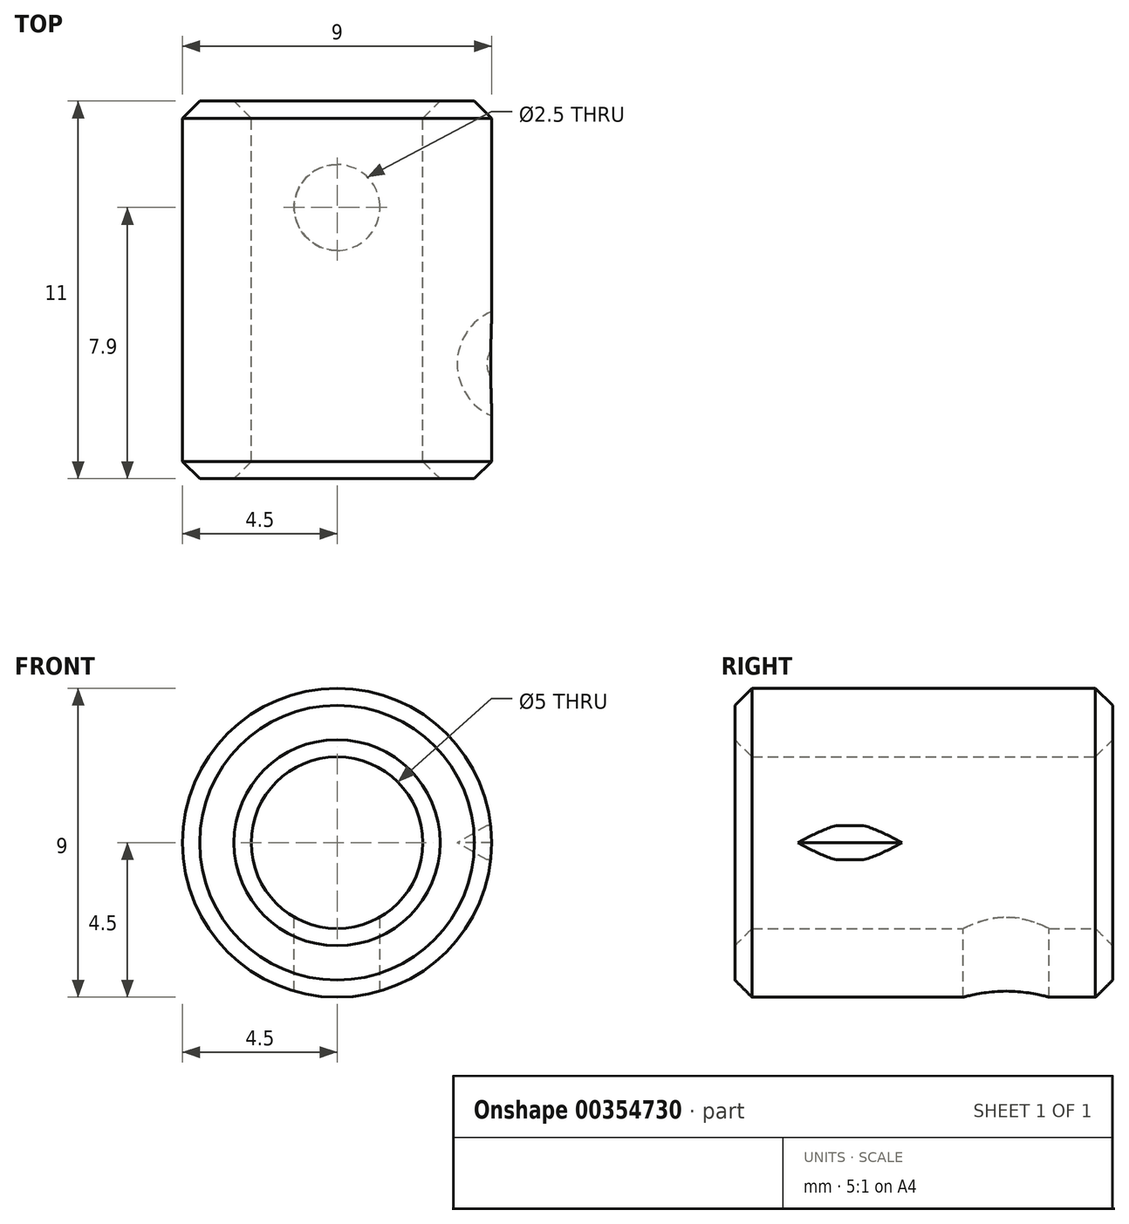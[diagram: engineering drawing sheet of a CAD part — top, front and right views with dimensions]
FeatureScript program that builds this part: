
annotation { "Feature Type Name" : "Feature", "Feature Type Description" : "" }
export const myFeature = defineFeature(function(context is Context, id is Id, definition is map)
    precondition{}
    {
        {
            var Q0;
            Q0=qCreatedBy(makeId("Front.planeOp"),FACE);
            var sketch = newSketch(context, id + "F0", { "sketchPlane" : qUnion([Q0])});
            skCircle(sketch, "E0", {"center": v(0, 0) * mm, "radius": 4.5 * mm});
            skCircle(sketch, "E1", {"center": v(0, 0) * mm, "radius": 2.5 * mm});
            skSolve(sketch);
        }
        {
            var Q0;
            Q0=qSketchRegion(id+"F0",true);
            extrude(context, id + "F1", {"entities" : qUnion([Q0]), "depth" : 11 * mm});
        }
        {
            var Q0;
            Q0=qCreatedBy(makeId("Top.planeOp"),FACE);
            var sketch = newSketch(context, id + "F2", { "sketchPlane" : qUnion([Q0])});
            skCircle(sketch, "E2", {"center": v(5.15, -7.65) * mm, "radius": 1.65 * mm});
            skLineSegment(sketch, "E3", {"start": v(0, -26.8) * mm, "end": v(0, 9.04) * mm, "construction": true});
            skSolve(sketch);
        }
        {
            var Q0;
            Q0=qSketchRegion(id+"F2",true);
            extrude(context, id + "F3", {"entities" : qUnion([Q0]), "endBound" : BoundingType.SYMMETRIC, "depth" : 1 * mm, "hasDraft" : true, "draftAngle" : 60 * degree, "draftPullDirection" : true});
        }
        {
            var Q0;
            Q0=makeQuery(id+"FlCykohCmPU6IM3_2.11.F3.*.split.splitOp","SPLIT",BODY,{"derivedFrom":makeQuery(id+"FlCykohCmPU6IM3_2.11.F3.opExtrude","SWEPT_BODY",BODY,{"disambiguationData":[OSD([sQuery(id+"F2.wireOp",EDGE,"E2")])]})});
            var Q1;
            Q1=makeQuery(id+"FlCykohCmPU6IM3_2.2.F3.*.split.splitOp","SPLIT",BODY,{"derivedFrom":makeQuery(id+"FlCykohCmPU6IM3_2.2.F3.opExtrude","SWEPT_BODY",BODY,{"disambiguationData":[OSD([sQuery(id+"F2.wireOp",EDGE,"E2")])]})});
            var Q2;
            Q2=makeQuery(id+"FlCykohCmPU6IM3_2.1.F3.*.split.splitOp","SPLIT",BODY,{"derivedFrom":makeQuery(id+"FlCykohCmPU6IM3_2.1.F3.opExtrude","SWEPT_BODY",BODY,{"disambiguationData":[OSD([sQuery(id+"F2.wireOp",EDGE,"E2")])]})});
            var Q3;
            Q3=makeQuery(id+"FlCykohCmPU6IM3_2.10.F3.*.split.splitOp","SPLIT",BODY,{"derivedFrom":makeQuery(id+"FlCykohCmPU6IM3_2.10.F3.opExtrude","SWEPT_BODY",BODY,{"disambiguationData":[OSD([sQuery(id+"F2.wireOp",EDGE,"E2")])]})});
            var Q4;
            Q4=makeQuery(id+"FlCykohCmPU6IM3_2.13.F3.*.split.splitOp","SPLIT",BODY,{"derivedFrom":makeQuery(id+"FlCykohCmPU6IM3_2.13.F3.opExtrude","SWEPT_BODY",BODY,{"disambiguationData":[OSD([sQuery(id+"F2.wireOp",EDGE,"E2")])]})});
            var Q5;
            Q5=makeQuery(id+"FlCykohCmPU6IM3_2.5.F3.*.split.splitOp","SPLIT",BODY,{"derivedFrom":makeQuery(id+"FlCykohCmPU6IM3_2.5.F3.opExtrude","SWEPT_BODY",BODY,{"disambiguationData":[OSD([sQuery(id+"F2.wireOp",EDGE,"E2")])]})});
            var Q6;
            Q6=makeQuery(id+"FlCykohCmPU6IM3_2.9.F3.*.split.splitOp","SPLIT",BODY,{"derivedFrom":makeQuery(id+"FlCykohCmPU6IM3_2.9.F3.opExtrude","SWEPT_BODY",BODY,{"disambiguationData":[OSD([sQuery(id+"F2.wireOp",EDGE,"E2")])]})});
            var Q7;
            Q7=makeQuery(id+"FlCykohCmPU6IM3_2.6.F3.*.split.splitOp","SPLIT",BODY,{"derivedFrom":makeQuery(id+"FlCykohCmPU6IM3_2.6.F3.opExtrude","SWEPT_BODY",BODY,{"disambiguationData":[OSD([sQuery(id+"F2.wireOp",EDGE,"E2")])]})});
            var Q8;
            Q8=makeQuery(id+"FlCykohCmPU6IM3_2.14.F3.*.split.splitOp","SPLIT",BODY,{"derivedFrom":makeQuery(id+"FlCykohCmPU6IM3_2.14.F3.opExtrude","SWEPT_BODY",BODY,{"disambiguationData":[OSD([sQuery(id+"F2.wireOp",EDGE,"E2")])]})});
            var Q9;
            Q9=makeQuery(id+"FlCykohCmPU6IM3_2.19.F3.*.split.splitOp","SPLIT",BODY,{"derivedFrom":makeQuery(id+"FlCykohCmPU6IM3_2.19.F3.opExtrude","SWEPT_BODY",BODY,{"disambiguationData":[OSD([sQuery(id+"F2.wireOp",EDGE,"E2")])]})});
            var Q10;
            Q10=makeQuery(id+"FlCykohCmPU6IM3_2.4.F3.*.split.splitOp","SPLIT",BODY,{"derivedFrom":makeQuery(id+"FlCykohCmPU6IM3_2.4.F3.opExtrude","SWEPT_BODY",BODY,{"disambiguationData":[OSD([sQuery(id+"F2.wireOp",EDGE,"E2")])]})});
            var Q11;
            Q11=makeQuery(id+"F3.*.split.splitOp","SPLIT",BODY,{"derivedFrom":makeQuery(id+"F3.opExtrude","SWEPT_BODY",BODY,{"disambiguationData":[OSD([sQuery(id+"F2.wireOp",EDGE,"E2")])]})});
            var Q12;
            Q12=makeQuery(id+"FlCykohCmPU6IM3_2.3.F3.*.split.splitOp","SPLIT",BODY,{"derivedFrom":makeQuery(id+"FlCykohCmPU6IM3_2.3.F3.opExtrude","SWEPT_BODY",BODY,{"disambiguationData":[OSD([sQuery(id+"F2.wireOp",EDGE,"E2")])]})});
            var Q13;
            Q13=makeQuery(id+"FlCykohCmPU6IM3_2.7.F3.*.split.splitOp","SPLIT",BODY,{"derivedFrom":makeQuery(id+"FlCykohCmPU6IM3_2.7.F3.opExtrude","SWEPT_BODY",BODY,{"disambiguationData":[OSD([sQuery(id+"F2.wireOp",EDGE,"E2")])]})});
            var Q14;
            Q14=makeQuery(id+"FlCykohCmPU6IM3_2.33.F3.*.split.splitOp","SPLIT",BODY,{"derivedFrom":makeQuery(id+"FlCykohCmPU6IM3_2.33.F3.opExtrude","SWEPT_BODY",BODY,{"disambiguationData":[OSD([sQuery(id+"F2.wireOp",EDGE,"E2")])]})});
            var Q15;
            Q15=makeQuery(id+"FlCykohCmPU6IM3_2.32.F3.*.split.splitOp","SPLIT",BODY,{"derivedFrom":makeQuery(id+"FlCykohCmPU6IM3_2.32.F3.opExtrude","SWEPT_BODY",BODY,{"disambiguationData":[OSD([sQuery(id+"F2.wireOp",EDGE,"E2")])]})});
            var Q16;
            Q16=makeQuery(id+"FlCykohCmPU6IM3_2.31.F3.*.split.splitOp","SPLIT",BODY,{"derivedFrom":makeQuery(id+"FlCykohCmPU6IM3_2.31.F3.opExtrude","SWEPT_BODY",BODY,{"disambiguationData":[OSD([sQuery(id+"F2.wireOp",EDGE,"E2")])]})});
            var Q17;
            Q17=makeQuery(id+"FlCykohCmPU6IM3_2.30.F3.*.split.splitOp","SPLIT",BODY,{"derivedFrom":makeQuery(id+"FlCykohCmPU6IM3_2.30.F3.opExtrude","SWEPT_BODY",BODY,{"disambiguationData":[OSD([sQuery(id+"F2.wireOp",EDGE,"E2")])]})});
            var Q18;
            Q18=makeQuery(id+"FlCykohCmPU6IM3_2.29.F3.*.split.splitOp","SPLIT",BODY,{"derivedFrom":makeQuery(id+"FlCykohCmPU6IM3_2.29.F3.opExtrude","SWEPT_BODY",BODY,{"disambiguationData":[OSD([sQuery(id+"F2.wireOp",EDGE,"E2")])]})});
            var Q19;
            Q19=makeQuery(id+"FlCykohCmPU6IM3_2.28.F3.*.split.splitOp","SPLIT",BODY,{"derivedFrom":makeQuery(id+"FlCykohCmPU6IM3_2.28.F3.opExtrude","SWEPT_BODY",BODY,{"disambiguationData":[OSD([sQuery(id+"F2.wireOp",EDGE,"E2")])]})});
            var Q20;
            Q20=makeQuery(id+"FlCykohCmPU6IM3_2.27.F3.*.split.splitOp","SPLIT",BODY,{"derivedFrom":makeQuery(id+"FlCykohCmPU6IM3_2.27.F3.opExtrude","SWEPT_BODY",BODY,{"disambiguationData":[OSD([sQuery(id+"F2.wireOp",EDGE,"E2")])]})});
            var Q21;
            Q21=makeQuery(id+"FlCykohCmPU6IM3_2.26.F3.*.split.splitOp","SPLIT",BODY,{"derivedFrom":makeQuery(id+"FlCykohCmPU6IM3_2.26.F3.opExtrude","SWEPT_BODY",BODY,{"disambiguationData":[OSD([sQuery(id+"F2.wireOp",EDGE,"E2")])]})});
            var Q22;
            Q22=makeQuery(id+"FlCykohCmPU6IM3_2.25.F3.*.split.splitOp","SPLIT",BODY,{"derivedFrom":makeQuery(id+"FlCykohCmPU6IM3_2.25.F3.opExtrude","SWEPT_BODY",BODY,{"disambiguationData":[OSD([sQuery(id+"F2.wireOp",EDGE,"E2")])]})});
            var Q23;
            Q23=makeQuery(id+"FlCykohCmPU6IM3_2.24.F3.*.split.splitOp","SPLIT",BODY,{"derivedFrom":makeQuery(id+"FlCykohCmPU6IM3_2.24.F3.opExtrude","SWEPT_BODY",BODY,{"disambiguationData":[OSD([sQuery(id+"F2.wireOp",EDGE,"E2")])]})});
            var Q24;
            Q24=makeQuery(id+"FlCykohCmPU6IM3_2.23.F3.*.split.splitOp","SPLIT",BODY,{"derivedFrom":makeQuery(id+"FlCykohCmPU6IM3_2.23.F3.opExtrude","SWEPT_BODY",BODY,{"disambiguationData":[OSD([sQuery(id+"F2.wireOp",EDGE,"E2")])]})});
            var Q25;
            Q25=makeQuery(id+"FlCykohCmPU6IM3_2.22.F3.*.split.splitOp","SPLIT",BODY,{"derivedFrom":makeQuery(id+"FlCykohCmPU6IM3_2.22.F3.opExtrude","SWEPT_BODY",BODY,{"disambiguationData":[OSD([sQuery(id+"F2.wireOp",EDGE,"E2")])]})});
            var Q26;
            Q26=makeQuery(id+"FlCykohCmPU6IM3_2.21.F3.*.split.splitOp","SPLIT",BODY,{"derivedFrom":makeQuery(id+"FlCykohCmPU6IM3_2.21.F3.opExtrude","SWEPT_BODY",BODY,{"disambiguationData":[OSD([sQuery(id+"F2.wireOp",EDGE,"E2")])]})});
            var Q27;
            Q27=makeQuery(id+"FlCykohCmPU6IM3_2.20.F3.*.split.splitOp","SPLIT",BODY,{"derivedFrom":makeQuery(id+"FlCykohCmPU6IM3_2.20.F3.opExtrude","SWEPT_BODY",BODY,{"disambiguationData":[OSD([sQuery(id+"F2.wireOp",EDGE,"E2")])]})});
            var Q28;
            Q28=makeQuery(id+"FlCykohCmPU6IM3_2.12.F3.*.split.splitOp","SPLIT",BODY,{"derivedFrom":makeQuery(id+"FlCykohCmPU6IM3_2.12.F3.opExtrude","SWEPT_BODY",BODY,{"disambiguationData":[OSD([sQuery(id+"F2.wireOp",EDGE,"E2")])]})});
            var Q29;
            Q29=makeQuery(id+"FlCykohCmPU6IM3_2.8.F3.*.split.splitOp","SPLIT",BODY,{"derivedFrom":makeQuery(id+"FlCykohCmPU6IM3_2.8.F3.opExtrude","SWEPT_BODY",BODY,{"disambiguationData":[OSD([sQuery(id+"F2.wireOp",EDGE,"E2")])]})});
            var Q30;
            Q30=makeQuery(id+"FlCykohCmPU6IM3_2.16.F3.*.split.splitOp","SPLIT",BODY,{"derivedFrom":makeQuery(id+"FlCykohCmPU6IM3_2.16.F3.opExtrude","SWEPT_BODY",BODY,{"disambiguationData":[OSD([sQuery(id+"F2.wireOp",EDGE,"E2")])]})});
            var Q31;
            Q31=makeQuery(id+"FlCykohCmPU6IM3_2.15.F3.*.split.splitOp","SPLIT",BODY,{"derivedFrom":makeQuery(id+"FlCykohCmPU6IM3_2.15.F3.opExtrude","SWEPT_BODY",BODY,{"disambiguationData":[OSD([sQuery(id+"F2.wireOp",EDGE,"E2")])]})});
            var Q32;
            Q32=makeQuery(id+"FlCykohCmPU6IM3_2.17.F3.*.split.splitOp","SPLIT",BODY,{"derivedFrom":makeQuery(id+"FlCykohCmPU6IM3_2.17.F3.opExtrude","SWEPT_BODY",BODY,{"disambiguationData":[OSD([sQuery(id+"F2.wireOp",EDGE,"E2")])]})});
            var Q33;
            Q33=makeQuery(id+"FlCykohCmPU6IM3_2.18.F3.*.split.splitOp","SPLIT",BODY,{"derivedFrom":makeQuery(id+"FlCykohCmPU6IM3_2.18.F3.opExtrude","SWEPT_BODY",BODY,{"disambiguationData":[OSD([sQuery(id+"F2.wireOp",EDGE,"E2")])]})});
            var Q34;
            Q34=makeQuery(id+"FlCykohCmPU6IM3_2.34.F3.*.split.splitOp","SPLIT",BODY,{"derivedFrom":makeQuery(id+"FlCykohCmPU6IM3_2.34.F3.opExtrude","SWEPT_BODY",BODY,{"disambiguationData":[OSD([sQuery(id+"F2.wireOp",EDGE,"E2")])]})});
            var Q35;
            Q35=makeQuery(id+"FlCykohCmPU6IM3_2.47.F3.*.split.splitOp","SPLIT",BODY,{"derivedFrom":makeQuery(id+"FlCykohCmPU6IM3_2.47.F3.opExtrude","SWEPT_BODY",BODY,{"disambiguationData":[OSD([sQuery(id+"F2.wireOp",EDGE,"E2")])]})});
            var Q36;
            Q36=makeQuery(id+"FlCykohCmPU6IM3_2.35.F3.*.split.splitOp","SPLIT",BODY,{"derivedFrom":makeQuery(id+"FlCykohCmPU6IM3_2.35.F3.opExtrude","SWEPT_BODY",BODY,{"disambiguationData":[OSD([sQuery(id+"F2.wireOp",EDGE,"E2")])]})});
            var Q37;
            Q37=makeQuery(id+"FlCykohCmPU6IM3_2.40.F3.*.split.splitOp","SPLIT",BODY,{"derivedFrom":makeQuery(id+"FlCykohCmPU6IM3_2.40.F3.opExtrude","SWEPT_BODY",BODY,{"disambiguationData":[OSD([sQuery(id+"F2.wireOp",EDGE,"E2")])]})});
            var Q38;
            Q38=makeQuery(id+"FlCykohCmPU6IM3_2.42.F3.*.split.splitOp","SPLIT",BODY,{"derivedFrom":makeQuery(id+"FlCykohCmPU6IM3_2.42.F3.opExtrude","SWEPT_BODY",BODY,{"disambiguationData":[OSD([sQuery(id+"F2.wireOp",EDGE,"E2")])]})});
            var Q39;
            Q39=makeQuery(id+"FlCykohCmPU6IM3_2.39.F3.*.split.splitOp","SPLIT",BODY,{"derivedFrom":makeQuery(id+"FlCykohCmPU6IM3_2.39.F3.opExtrude","SWEPT_BODY",BODY,{"disambiguationData":[OSD([sQuery(id+"F2.wireOp",EDGE,"E2")])]})});
            var Q40;
            Q40=makeQuery(id+"FlCykohCmPU6IM3_2.44.F3.*.split.splitOp","SPLIT",BODY,{"derivedFrom":makeQuery(id+"FlCykohCmPU6IM3_2.44.F3.opExtrude","SWEPT_BODY",BODY,{"disambiguationData":[OSD([sQuery(id+"F2.wireOp",EDGE,"E2")])]})});
            var Q41;
            Q41=makeQuery(id+"FlCykohCmPU6IM3_2.46.F3.*.split.splitOp","SPLIT",BODY,{"derivedFrom":makeQuery(id+"FlCykohCmPU6IM3_2.46.F3.opExtrude","SWEPT_BODY",BODY,{"disambiguationData":[OSD([sQuery(id+"F2.wireOp",EDGE,"E2")])]})});
            var Q42;
            Q42=makeQuery(id+"FlCykohCmPU6IM3_2.45.F3.*.split.splitOp","SPLIT",BODY,{"derivedFrom":makeQuery(id+"FlCykohCmPU6IM3_2.45.F3.opExtrude","SWEPT_BODY",BODY,{"disambiguationData":[OSD([sQuery(id+"F2.wireOp",EDGE,"E2")])]})});
            var Q43;
            Q43=makeQuery(id+"FlCykohCmPU6IM3_2.38.F3.*.split.splitOp","SPLIT",BODY,{"derivedFrom":makeQuery(id+"FlCykohCmPU6IM3_2.38.F3.opExtrude","SWEPT_BODY",BODY,{"disambiguationData":[OSD([sQuery(id+"F2.wireOp",EDGE,"E2")])]})});
            var Q44;
            Q44=makeQuery(id+"FlCykohCmPU6IM3_2.36.F3.*.split.splitOp","SPLIT",BODY,{"derivedFrom":makeQuery(id+"FlCykohCmPU6IM3_2.36.F3.opExtrude","SWEPT_BODY",BODY,{"disambiguationData":[OSD([sQuery(id+"F2.wireOp",EDGE,"E2")])]})});
            var Q45;
            Q45=makeQuery(id+"FlCykohCmPU6IM3_2.37.F3.*.split.splitOp","SPLIT",BODY,{"derivedFrom":makeQuery(id+"FlCykohCmPU6IM3_2.37.F3.opExtrude","SWEPT_BODY",BODY,{"disambiguationData":[OSD([sQuery(id+"F2.wireOp",EDGE,"E2")])]})});
            var Q46;
            Q46=makeQuery(id+"FlCykohCmPU6IM3_2.48.F3.*.split.splitOp","SPLIT",BODY,{"derivedFrom":makeQuery(id+"FlCykohCmPU6IM3_2.48.F3.opExtrude","SWEPT_BODY",BODY,{"disambiguationData":[OSD([sQuery(id+"F2.wireOp",EDGE,"E2")])]})});
            var Q47;
            Q47=makeQuery(id+"FlCykohCmPU6IM3_2.41.F3.*.split.splitOp","SPLIT",BODY,{"derivedFrom":makeQuery(id+"FlCykohCmPU6IM3_2.41.F3.opExtrude","SWEPT_BODY",BODY,{"disambiguationData":[OSD([sQuery(id+"F2.wireOp",EDGE,"E2")])]})});
            var Q48;
            Q48=makeQuery(id+"FlCykohCmPU6IM3_2.43.F3.*.split.splitOp","SPLIT",BODY,{"derivedFrom":makeQuery(id+"FlCykohCmPU6IM3_2.43.F3.opExtrude","SWEPT_BODY",BODY,{"disambiguationData":[OSD([sQuery(id+"F2.wireOp",EDGE,"E2")])]})});
            var Q49;
            Q49=makeQuery(id+"FlCykohCmPU6IM3_2.59.F3.*.split.splitOp","SPLIT",BODY,{"derivedFrom":makeQuery(id+"FlCykohCmPU6IM3_2.59.F3.opExtrude","SWEPT_BODY",BODY,{"disambiguationData":[OSD([sQuery(id+"F2.wireOp",EDGE,"E2")])]})});
            var Q50;
            Q50=makeQuery(id+"FlCykohCmPU6IM3_2.58.F3.*.split.splitOp","SPLIT",BODY,{"derivedFrom":makeQuery(id+"FlCykohCmPU6IM3_2.58.F3.opExtrude","SWEPT_BODY",BODY,{"disambiguationData":[OSD([sQuery(id+"F2.wireOp",EDGE,"E2")])]})});
            var Q51;
            Q51=makeQuery(id+"FlCykohCmPU6IM3_2.57.F3.*.split.splitOp","SPLIT",BODY,{"derivedFrom":makeQuery(id+"FlCykohCmPU6IM3_2.57.F3.opExtrude","SWEPT_BODY",BODY,{"disambiguationData":[OSD([sQuery(id+"F2.wireOp",EDGE,"E2")])]})});
            var Q52;
            Q52=makeQuery(id+"FlCykohCmPU6IM3_2.56.F3.*.split.splitOp","SPLIT",BODY,{"derivedFrom":makeQuery(id+"FlCykohCmPU6IM3_2.56.F3.opExtrude","SWEPT_BODY",BODY,{"disambiguationData":[OSD([sQuery(id+"F2.wireOp",EDGE,"E2")])]})});
            var Q53;
            Q53=makeQuery(id+"FlCykohCmPU6IM3_2.55.F3.*.split.splitOp","SPLIT",BODY,{"derivedFrom":makeQuery(id+"FlCykohCmPU6IM3_2.55.F3.opExtrude","SWEPT_BODY",BODY,{"disambiguationData":[OSD([sQuery(id+"F2.wireOp",EDGE,"E2")])]})});
            var Q54;
            Q54=makeQuery(id+"FlCykohCmPU6IM3_2.54.F3.*.split.splitOp","SPLIT",BODY,{"derivedFrom":makeQuery(id+"FlCykohCmPU6IM3_2.54.F3.opExtrude","SWEPT_BODY",BODY,{"disambiguationData":[OSD([sQuery(id+"F2.wireOp",EDGE,"E2")])]})});
            var Q55;
            Q55=makeQuery(id+"FlCykohCmPU6IM3_2.53.F3.*.split.splitOp","SPLIT",BODY,{"derivedFrom":makeQuery(id+"FlCykohCmPU6IM3_2.53.F3.opExtrude","SWEPT_BODY",BODY,{"disambiguationData":[OSD([sQuery(id+"F2.wireOp",EDGE,"E2")])]})});
            var Q56;
            Q56=makeQuery(id+"FlCykohCmPU6IM3_2.52.F3.*.split.splitOp","SPLIT",BODY,{"derivedFrom":makeQuery(id+"FlCykohCmPU6IM3_2.52.F3.opExtrude","SWEPT_BODY",BODY,{"disambiguationData":[OSD([sQuery(id+"F2.wireOp",EDGE,"E2")])]})});
            var Q57;
            Q57=makeQuery(id+"FlCykohCmPU6IM3_2.51.F3.*.split.splitOp","SPLIT",BODY,{"derivedFrom":makeQuery(id+"FlCykohCmPU6IM3_2.51.F3.opExtrude","SWEPT_BODY",BODY,{"disambiguationData":[OSD([sQuery(id+"F2.wireOp",EDGE,"E2")])]})});
            var Q58;
            Q58=makeQuery(id+"FlCykohCmPU6IM3_2.50.F3.*.split.splitOp","SPLIT",BODY,{"derivedFrom":makeQuery(id+"FlCykohCmPU6IM3_2.50.F3.opExtrude","SWEPT_BODY",BODY,{"disambiguationData":[OSD([sQuery(id+"F2.wireOp",EDGE,"E2")])]})});
            var Q59;
            Q59=makeQuery(id+"FlCykohCmPU6IM3_2.49.F3.*.split.splitOp","SPLIT",BODY,{"derivedFrom":makeQuery(id+"FlCykohCmPU6IM3_2.49.F3.opExtrude","SWEPT_BODY",BODY,{"disambiguationData":[OSD([sQuery(id+"F2.wireOp",EDGE,"E2")])]})});
            var Q60;
            Q60=makeQuery(id+"F1.opExtrude","SWEPT_BODY",BODY,{"disambiguationData":[OSD([sQuery(id+"F0.wireOp",EDGE,"E0"),sQuery(id+"F0.wireOp",EDGE,"E1")])]});
            booleanBodies(context, id + "F4", {"operationType" : BooleanOperationType.SUBTRACTION, "tools" : qUnion([Q0, Q1, Q2, Q3, Q4, Q5, Q6, Q7, Q8, Q9, Q10, Q11, Q12, Q13, Q14, Q15, Q16, Q17, Q18, Q19, Q20, Q21, Q22, Q23, Q24, Q25, Q26, Q27, Q28, Q29, Q30, Q31, Q32, Q33, Q34, Q35, Q36, Q37, Q38, Q39, Q40, Q41, Q42, Q43, Q44, Q45, Q46, Q47, Q48, Q49, Q50, Q51, Q52, Q53, Q54, Q55, Q56, Q57, Q58, Q59]), "targets" : qUnion([Q60])});
        }
        {
            var Q0;
            Q0=qCreatedBy(makeId("Top.planeOp"),FACE);
            var sketch = newSketch(context, id + "F5", { "sketchPlane" : qUnion([Q0])});
            skCircle(sketch, "E4", {"center": v(0, -3.1) * mm, "radius": 1.25 * mm});
            skSolve(sketch);
        }
        {
            var Q0;
            Q0=qSketchRegion(id+"F5",true);
            var Q1;
            {var subQ0=sQuery(id+"F0.wireOp",EDGE,"E0");Q1=makeQuery(id+"FioVggKPFHV3JOt_1.boolean.opBoolean","SPLIT",FACE,{"disambiguationData":[TD([makeQuery(id+"F1.opExtrude","CAP_FACE",FACE,{"disambiguationData":[OSD([subQ0,sQuery(id+"F0.wireOp",EDGE,"E1")])],"isStart":true})])],"derivedFrom":makeQuery(id+"F1.opExtrude","SWEPT_FACE",FACE,{"disambiguationData":[OSD([subQ0])]})});}
            extrude(context, id + "F6", {"entities" : qUnion([Q0]), "operationType" : NewBodyOperationType.REMOVE, "endBound" : BoundingType.UP_TO_SURFACE, "oppositeDirection" : true, "endBoundEntityFace" : qUnion([Q1]), "depth" : 25 * mm});
        }
        {
            var Q0;
            Q0=makeQuery(id+"F1.opExtrude","CAP_EDGE",EDGE,{"disambiguationData":[OSD([sQuery(id+"F0.wireOp",EDGE,"E0")])],"isStart":false});
            var Q1;
            Q1=makeQuery(id+"F1.opExtrude","CAP_EDGE",EDGE,{"disambiguationData":[OSD([sQuery(id+"F0.wireOp",EDGE,"E1")])],"isStart":false});
            var Q2;
            Q2=makeQuery(id+"F1.opExtrude","CAP_EDGE",EDGE,{"disambiguationData":[OSD([sQuery(id+"F0.wireOp",EDGE,"E1")])],"isStart":true});
            var Q3;
            Q3=makeQuery(id+"F1.opExtrude","CAP_EDGE",EDGE,{"disambiguationData":[OSD([sQuery(id+"F0.wireOp",EDGE,"E0")])],"isStart":true});
            chamfer(context, id + "F7", {"entities" : qUnion([Q0, Q1, Q2, Q3]), "width" : .5 * mm, "tangentPropagation" : true});
        }
    });
